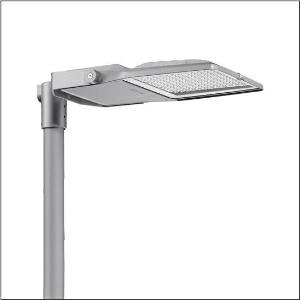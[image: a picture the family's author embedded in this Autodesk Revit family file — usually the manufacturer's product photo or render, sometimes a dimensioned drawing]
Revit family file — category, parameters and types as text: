
# Revit family: floodlight_fl_21_iq_midi___pl43_5xa7781e4a3a_24f4
name_source: partatom
category: Lighting Fixtures
units: mm (PartAtom-declared; Revit-internal decimal feet)

## family parameters
Cut with Voids When Loaded = No
Host = Face
Light Source = No
Part Type = Normal
Room Calculation Point = No
Round Connector Dimension = Use Diameter
Shared = No

## types (1)
- --- (1 x LED, 28730 lm, 208.1 W, 4000K)
    Apparent Load = 208 VA
    CIE Flux Codes = 27 78 99 100 100
    Color Rendering = 70
    Color Temperature = 4000K
    Default Elevation = 1800 mm
    Description = Floodlight FL 21 iQ midi, floodlight, primary light control with lens, of PMMA, primary optical cover: protective disc, of toughened safety glass, transparent, light distribution: PL43, light emission: direct distribution, installation type: surface-mounted, LED, High Power LED, rated luminous flux: 28.730lm, luminous efficacy: 138lm/W, light colour: 740, colour temperature: 4000K, control gear: ECG iQ, control: optimised constant luminous flux control (CLO 2.0), Desk-Remote (wireless, voltage-free reading and setting of iQ features in the workshop via application-optimized NFC function/RFID function), Light-Fading, Smart-Wire, Night-Set, Lumen-Switch, Temp-Guard, Auto-Match, with terminal, 6-pole, mains connection: 220..240V, AC, 50/60Hz, start of lifetime: 208W, end of service life: 227W, reduction: 90W, luminaire housing, of diecast aluminium, powder-coated, Siteco® metallic grey (DB 702S), corrosivity category C5 mid according to DIN EN ISO 12944, sealing non-destructively replaceable, please order mast flange separately, mast bracket, of steel, galvanised, powder-coated, Siteco® metallic grey (DB 702S), protection rating (complete): IP66, insulation class (complete): insulation class II (safety insulation), certification: CE, protection symbol: D, impact resistance: IK08, permissible operating ambient temperature: -40..+40°C, permissible operating ambient temperature for outdoor applications: -40..+50°C, standard: DIN EN 12944, LABS conformity tested according to VDMA 24364:2018-05, packaging unit: 1 piece

Light Distribution: PL43
    Height = 76 mm
    Lamp = 1 x LED
    Lamp Light Flux = 28730 lm
    Lamp Power = 208.1 W
    Lamp count = 1
    Length = 657 mm
    Luminous efficacy = 138 lm/W
    Manufacturer = Siteco
    ModVariant = No
    Model = 5XA7781E4A3A
    Number of Poles = 1
    OnlyDefault = Yes
    Power Factor = 1
    Product Name = Floodlight FL 21 iQ midi | PL43
    Product group = floodlight | pylon annexe
    ProductGroupID = 6200
    Protection Class = Protection class II
    Protection Degree = IP 66
    RLX_Detail_Level = 1
    RLX_Emergency_Light_Flux = 0 lm
    RLX_Emergency_Type = 0
    RLX_Emergency_Type_DB = No
    RlxData = <blob elided: 153509 chars, md5=076d6bec>
    Socket = socket
    Standby Power = 0 W
    System Light Flux = 28730 lm
    System Power = 208 W
    Type Comments = factory setting: luminous flux: 100 % | dim-lin: 254 | 710 mA
    Type Image = l_1007123.jpg
    URL = http://relux.com
    VarID = @adj_053585
    Voltage = 0 V
    Weight = 0.00 kg
    Width = 442 mm

## geometry (parser evidence)
native form markers: Blend x4, Sweep x11
no freeform markers — native parametric forms only
